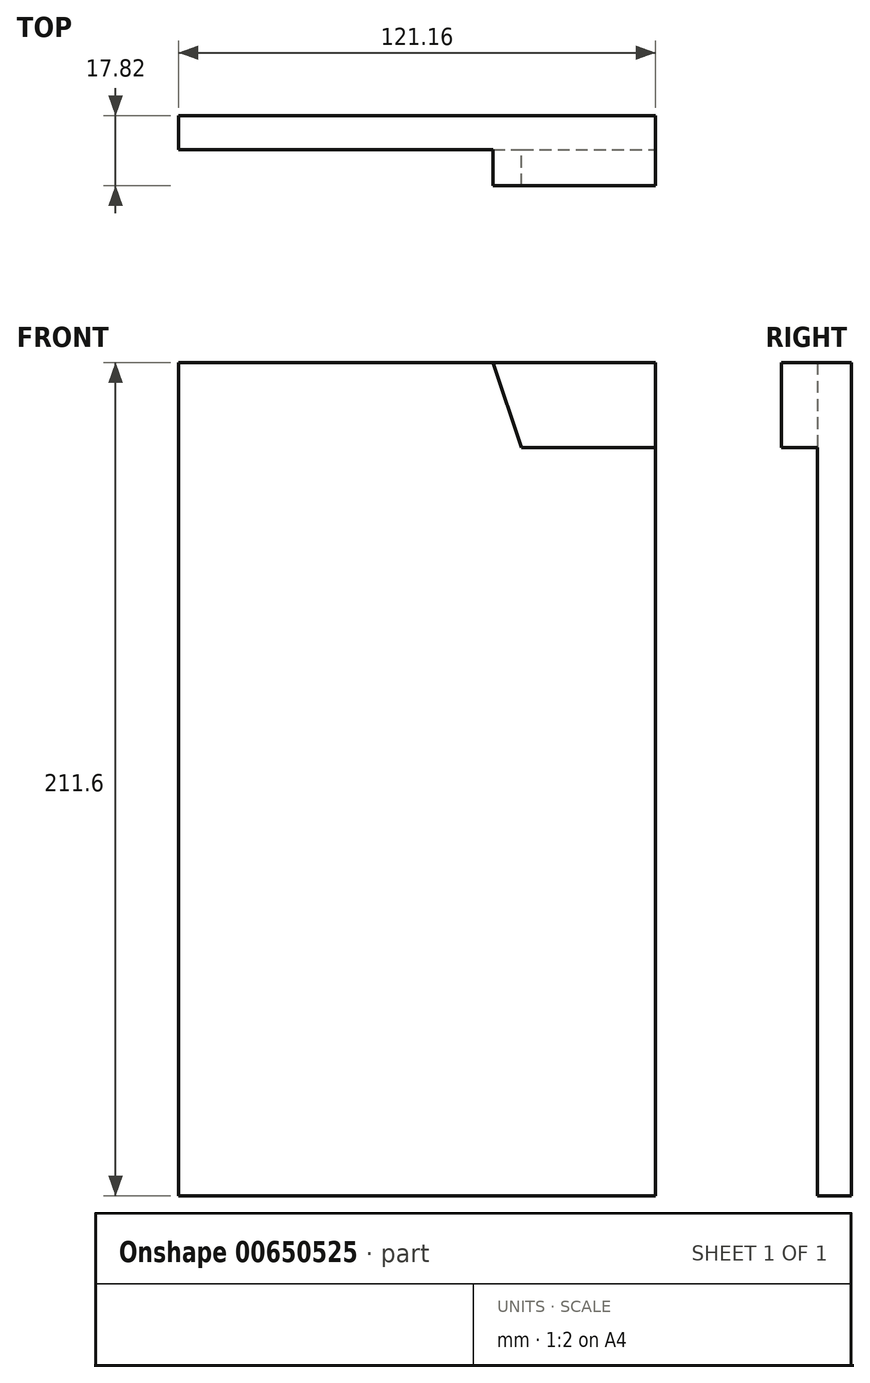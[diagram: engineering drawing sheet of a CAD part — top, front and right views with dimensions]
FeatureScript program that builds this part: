
annotation { "Feature Type Name" : "Feature", "Feature Type Description" : "" }
export const myFeature = defineFeature(function(context is Context, id is Id, definition is map)
    precondition{}
    {
        {
            var Q0;
            Q0=qCreatedBy(makeId("Front.planeOp"),FACE);
            var sketch = newSketch(context, id + "F0", { "sketchPlane" : qUnion([Q0])});
            skLineSegment(sketch, "E0.bottom", {"start": v(-60.58, -105.8) * mm, "end": v(60.58, -105.8) * mm});
            skLineSegment(sketch, "E0.top", {"start": v(-60.58, 105.8) * mm, "end": v(60.58, 105.8) * mm});
            skLineSegment(sketch, "E0.left", {"start": v(-60.58, -105.8) * mm, "end": v(-60.58, 105.8) * mm});
            skLineSegment(sketch, "E0.right", {"start": v(60.58, -105.8) * mm, "end": v(60.58, 105.8) * mm});
            skPoint(sketch, "E0.middle", {"position": v(0, 0) * mm});
            skSolve(sketch);
        }
        {
            var Q0;
            Q0=makeQuery(id+"F0.imprint","IMPRINT",FACE,{"disambiguationData":[TD([[makeQuery(id+"F0.imprint","IMPRINT",EDGE,{"derivedFrom":sQuery(id+"F0.wireOp",EDGE,"E0.bottom")}),1.0]])]});
            var sketch = newSketch(context, id + "F1", { "sketchPlane" : qUnion([Q0])});
            skSolve(sketch);
        }
        {
            var Q0;
            Q0=makeQuery(id+"F1.imprint","IMPRINT",FACE,{"disambiguationData":[TD([[makeQuery(id+"F1.imprint","IMPRINT",EDGE,{"derivedFrom":makeQuery(id+"F0.imprint","IMPRINT",EDGE,{"derivedFrom":sQuery(id+"F0.wireOp",EDGE,"E0.bottom")})}),1.0]])]});
            extrude(context, id + "F2", {"entities" : qUnion([Q0]), "depth" : 8.7 * mm, "offsetDistance" : 25.4 * mm});
        }
        {
            var Q0;
            Q0=makeQuery(id+"F2.opExtrude","CAP_FACE",FACE,{"disambiguationData":[OSD([sQuery(id+"F0.wireOp",EDGE,"E0.bottom"),sQuery(id+"F0.wireOp",EDGE,"E0.top"),sQuery(id+"F0.wireOp",EDGE,"E0.left"),sQuery(id+"F0.wireOp",EDGE,"E0.right")])],"isStart":false});
            var sketch = newSketch(context, id + "F3", { "sketchPlane" : qUnion([Q0])});
            skLineSegment(sketch, "E1", {"start": v(19.3, 105.8) * mm, "end": v(26.54, 84.33) * mm});
            skLineSegment(sketch, "E2", {"start": v(26.54, 84.33) * mm, "end": v(60.58, 84.33) * mm});
            skLineSegment(sketch, "E3", {"start": v(60.58, 84.33) * mm, "end": v(60.58, 105.8) * mm});
            skLineSegment(sketch, "E4", {"start": v(60.58, 105.8) * mm, "end": v(19.3, 105.8) * mm});
            skSolve(sketch);
        }
        {
            var Q0;
            Q0=makeQuery(id+"F3.imprint","IMPRINT",FACE,{"disambiguationData":[TD([[makeQuery(id+"F3.imprint","IMPRINT",EDGE,{"derivedFrom":sQuery(id+"F3.wireOp",EDGE,"E1")}),1.0]])]});
            extrude(context, id + "F4", {"entities" : qUnion([Q0]), "operationType" : NewBodyOperationType.ADD, "depth" : 9.13 * mm, "offsetDistance" : 25.4 * mm});
        }
    });
